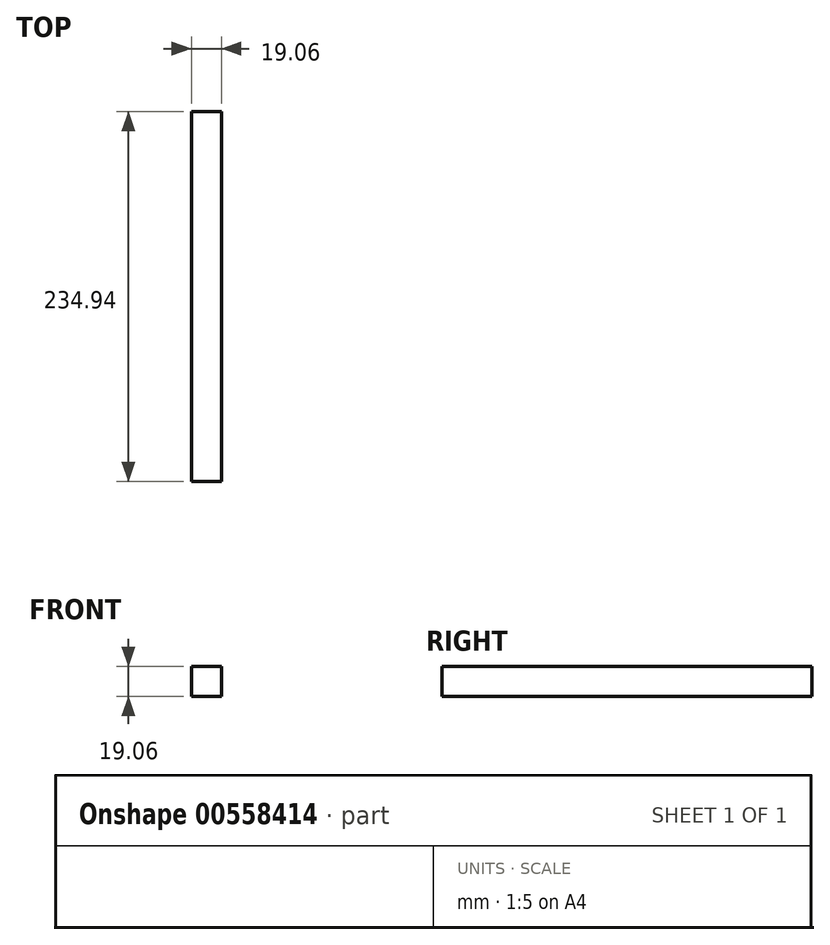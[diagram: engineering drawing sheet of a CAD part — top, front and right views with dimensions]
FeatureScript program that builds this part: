
annotation { "Feature Type Name" : "Feature", "Feature Type Description" : "" }
export const myFeature = defineFeature(function(context is Context, id is Id, definition is map)
    precondition{}
    {
        {
            var Q0;
            Q0=qCreatedBy(makeId("Top.planeOp"),FACE);
            var sketch = newSketch(context, id + "F0", { "sketchPlane" : qUnion([Q0])});
            skLineSegment(sketch, "E0.bottom", {"start": v(9.53, 117.48) * mm, "end": v(-9.52, 117.48) * mm});
            skLineSegment(sketch, "E0.top", {"start": v(9.52, -117.48) * mm, "end": v(-9.53, -117.48) * mm});
            skLineSegment(sketch, "E0.left", {"start": v(9.53, 117.48) * mm, "end": v(9.52, -117.48) * mm});
            skLineSegment(sketch, "E0.right", {"start": v(-9.52, 117.48) * mm, "end": v(-9.53, -117.48) * mm});
            skPoint(sketch, "E0.middle", {"position": v(0, 0) * mm});
            skSolve(sketch);
        }
        {
            var Q0;
            Q0=makeQuery(id+"F0.imprint","IMPRINT",FACE,{"disambiguationData":[TD([[makeQuery(id+"F0.imprint","IMPRINT",EDGE,{"derivedFrom":sQuery(id+"F0.wireOp",EDGE,"E0.bottom")}),1.0]])]});
            extrude(context, id + "F1", {"entities" : qUnion([Q0]), "endBound" : BoundingType.SYMMETRIC, "depth" : 19.05 * mm, "offsetDistance" : 25.4 * mm});
        }
    });
